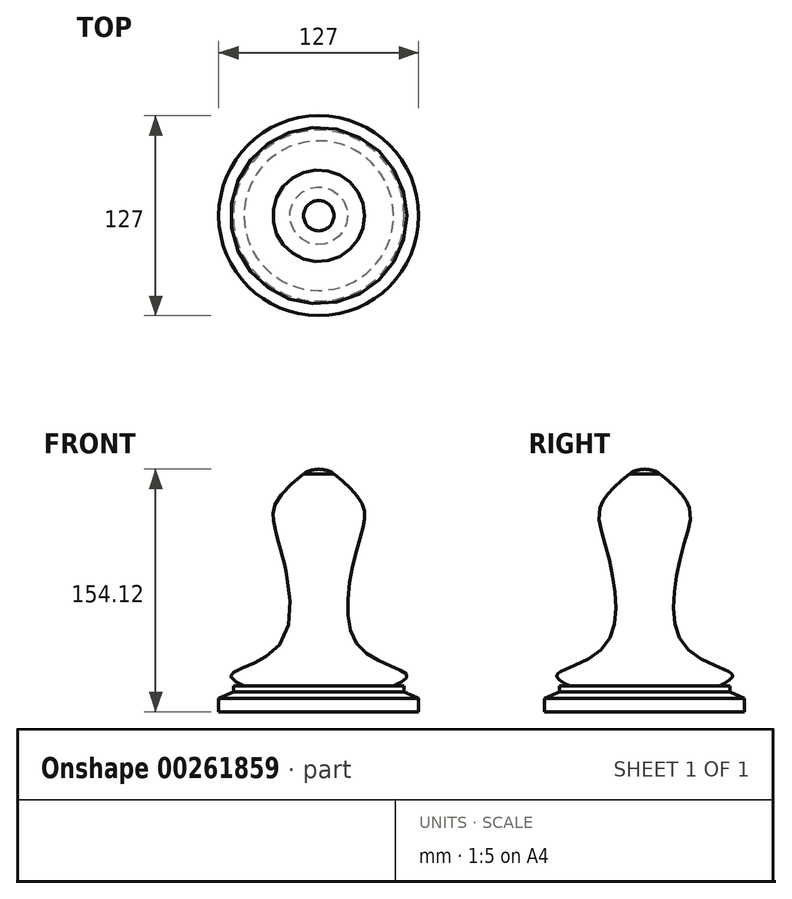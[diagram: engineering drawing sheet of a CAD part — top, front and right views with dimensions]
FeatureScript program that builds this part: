
annotation { "Feature Type Name" : "Feature", "Feature Type Description" : "" }
export const myFeature = defineFeature(function(context is Context, id is Id, definition is map)
    precondition{}
    {
        {
            var Q0;
            Q0=qCreatedBy(makeId("Front.planeOp"),FACE);
            var sketch = newSketch(context, id + "F0", { "sketchPlane" : qUnion([Q0])});
            skLineSegment(sketch, "E0", {"start": v(0, -76.32) * mm, "end": v(-63.5, -76.32) * mm});
            skLineSegment(sketch, "E1", {"start": v(-63.5, -76.32) * mm, "end": v(-63.5, -67.74) * mm});
            skLineSegment(sketch, "E2", {"start": v(-63.5, -67.74) * mm, "end": v(-54.26, -63.76) * mm});
            skLineSegment(sketch, "E3", {"start": v(-54.26, -63.76) * mm, "end": v(-54.26, -59.84) * mm});
            skLineSegment(sketch, "E4", {"start": v(-54.26, -59.84) * mm, "end": v(-47.51, -59.84) * mm});
            skFitSpline(sketch, "E5", {"points": [v(-47.51, -59.84) * mm, v(-55.9, -52.85) * mm, v(-24.73, -33.66) * mm, v(-25.44, 31.44) * mm, v(-27.94, 54.74) * mm, v(-7.88, 76.07) * mm], "startDerivative": vector(-124.3, 61.9) * mm, "endDerivative": vector(131.45, 100.5) * mm});
            skLineSegment(sketch, "E6", {"start": v(0, 76.07) * mm, "end": v(0, -76.32) * mm});
            skLineSegment(sketch, "E7", {"start": v(0, 74.76) * mm, "end": v(0, -76.32) * mm, "construction": true});
            skPoint(sketch, "E8.visualSharp", {"position": v(0, 76.07) * mm});
            skFitSpline(sketch, "E9", {"points": [v(-9.63, 74.72) * mm, v(-7.88, 76.07) * mm, v(-3.73, 77.26) * mm, v(0, 77.8) * mm], "startDerivative": vector(5.42, 5.32) * mm, "endDerivative": vector(10.12, 1.24) * mm});
            skLineSegment(sketch, "E10", {"start": v(0, 77.8) * mm, "end": v(0, 74.76) * mm});
            skSolve(sketch);
        }
        {
            var Q0;
            Q0=qCreatedBy(makeId("Front.planeOp"),FACE);
            var sketch = newSketch(context, id + "F1", { "sketchPlane" : qUnion([Q0])});
            skLineSegment(sketch, "E11", {"start": v(0, 75.5) * mm, "end": v(0, -76.95) * mm});
            skSolve(sketch);
        }
        {
            var Q0;
            Q0 = qSketchRegion(id + "F0", true);
            var Q1;
            Q1 = qSketchRegion(id + "F1", true);
            var Q2;
            Q2=sQuery(id+"F1.wireOp",EDGE,"E11");
            revolve(context, id + "F2", {"entities" : qUnion([Q0, Q1]), "axis" : qUnion([Q2]), "revolveType" : RevolveType.FULL});
        }
    });
